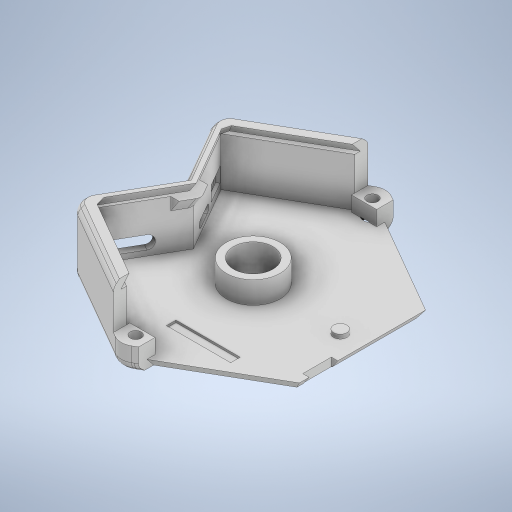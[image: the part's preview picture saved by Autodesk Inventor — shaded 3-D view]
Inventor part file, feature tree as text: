
AUTODESK INVENTOR PART (.ipt)
format: ipt  version: 2024 (Build 280153000, 153)  size: 1,012,224 bytes
history: native  units: in
note: dims shown in document units (in); Inventor stores cm internally (conversion verified against a paired STEP export)
features: extrude x30, move_body x17, direct_edit x9, draft x6, sketch x4, fillet x3, chamfer x2, plane x1
ambient origin geometry x8: Origin, YZ Plane, XZ Plane, XY Plane, X Axis, Y Axis, Z Axis, Center Point
bodies: Solid1 (feature_tree)
feature tree (72):
  extrude  "Extrusion1"  Depth=0.374in
  extrude  "Extrusion2"  Depth=0.0787in TaperAngle=0.0deg
  extrude  "Extrusion3"  Depth=0.6181in TaperAngle=0.0deg
  extrude  "Extrusion6"  Depth=0.0197in
  extrude  "Extrusion9"  Depth=0.0197in
  extrude  "Extrusion11"  Depth=0.0197in
  extrude  "Extrusion12"  Depth=0.0197in
  extrude  "Extrusion13"  TaperAngle=0.0deg  [1 undecoded]
  extrude  "Extrusion14"  Depth=0.0197in
  extrude  "Extrusion15"  Depth=0.0197in
  extrude  "Extrusion16"  Depth=0.0709in
  direct_edit  "Direct Edit2"
  direct_edit  "Direct Edit3"
  extrude  "Extrusion17"  Depth=0.0709in
  extrude  "Extrusion19"  Depth=0.0197in
  extrude  "Extrusion26"  Depth=0.0197in
  extrude  "Extrusion27"  TaperAngle=0.0deg  [1 undecoded]
  sketch  "Sketch19"  dims[d1=0.5098in d2=0.374in]
  extrude  "Extrusion28"  Depth=0.3937in TaperAngle=0.0deg
  extrude  "Extrusion29"  TaperAngle=0.0deg  [1 undecoded]
  draft  "FaceDraft1"
  draft  "FaceDraft2"
  draft  "FaceDraft4"
  sketch  "Sketch20"  dims[d3=0.4449in d7=0.0787in d8=0.0in]
  extrude  "Extrusion30"  Depth=0.3937in TaperAngle=0.0deg
  extrude  "Extrusion31"  Depth=0.0197in TaperAngle=0.0deg
  extrude  "Extrusion32"  Depth=0.0787in
  direct_edit  "Direct Edit5"
  plane  "Work Plane1"
  extrude  "Extrusion37"  Depth=0.0197in TaperAngle=0.0deg
  extrude  "Extrusion38"  Depth=0.0787in
  extrude  "Extrusion39"  Depth=0.0197in TaperAngle=0.0deg
  extrude  "Extrusion40"  Depth=0.0787in TaperAngle=0.0deg
  extrude  "Extrusion42"  TaperAngle=0.0deg  [1 undecoded]
  draft  "FaceDraft5"
  fillet  "Fillet1"  Radius=0.0787in
  draft  "FaceDraft6"
  chamfer  "Chamfer5"  [1 undecoded]
  fillet  "Fillet5"  Radius=0.2405in
  direct_edit  "Direct Edit8"
  direct_edit  "Direct Edit9"
  direct_edit  "Direct Edit10"
  extrude  "Extrusion43"  Depth=0.0787in
  direct_edit  "Direct Edit13"
  direct_edit  "Direct Edit14"
  direct_edit  "Direct Edit15"
  extrude  "Extrusion44"  TaperAngle=0.0deg  [1 undecoded]
  chamfer  "Chamfer6"  [1 undecoded]
  draft  "FaceDraft7"
  fillet  "Fillet6"  Radius=0.3937in
  extrude  "Extrusion45"  Depth=0.0787in
  sketch  "Sketch27"  dims[d21=0.1642in d22=0.1071in d23=0.1142in d24=0.2276in d25=0.1142in d26=0.0in d27=0.0in d38=0.1929in d40=0.1732in d42=0.0709in d43=0.0709in d44=0.6871in d45=0.6871in d46=0.0in d47=0.0in d51=0.3937in d52=0.0in d56=0.0in d57=0.0in d58=0.3937in d59=0.0in d60=0.3976in d61=0.0in d63=0.0787in d64=0.0689in d65=0.0in d66=0.0787in d67=0.0689in d68=0.0in d69=0.0in d70=0.0in d71=0.0787in d72=0.0in d73=0.0in d74=-0.0689in d80=0.0787in d81=0.0in d82=0.0in d85=0.2405in d86=0.0787in d87=0.0in d88=0.0in d118=0.0in d119=0.0in d120=0.3937in d121=0.0in d122=0.0787in d123=30.0deg d124=0.0in d125=0.0in d126=0.3937in d127=0.0in d128=0.2405in d129=-0.2405in d134=0.2405in d135=0.1693in d137=0.0827in d138=0.0in d139=0.0906in d140=0.0in d141=0.0984in d142=0.0in d144=120.0deg d148=0.1575in d154=90.0deg d160=0.1354in d161=0.1378in d179=0.126in d180=0.8268in d181=0.0394in d182=0.0in d183=0.1299in d184=0.1417in d185=0.3937in d186=0.0in d199=0.0in d200=0.0in d201=0.1417in d202=0.0984in d204=0.0394in d205=0.0in d207=120.0deg d211=0.0in d212=0.0in d213=30.0deg d214=-0.2061in d215=0.0492in d216=0.0787in d217=45.0deg d218=0.0787in d219=0.0157in d220=0.0118in d221=0.0in d222=0.0in d223=-0.0059in d224=0.1043in d226=0.0906in d228=0.0in d229=0.0in d230=0.0197in d231=0.0in d232=0.0in d233=-0.0197in d234=0.1535in d235=0.0079in d236=0.1535in d237=0.0906in d239=0.1043in d240=0.0079in d241=0.0295in d242=0.0433in d243=0.0315in d244=0.0335in d247=0.9695in d248=120.0deg d249=0.0295in d250=0.0433in d251=0.065in d253=60.0deg d254=0.0in d255=0.0in d256=0.0157in d258=0.3779in d260=45.0deg d261=45.0deg d262=0.0in d263=0.0in d264=0.0098in d265=0.0in d266=0.0in d267=0.0098in d268=0.1043in d269=0.3937in d270=0.0in d277=0.2224in d278=0.0in d279=0.0in d280=0.0079in d281=0.0in d282=0.0in d283=0.0079in d284=0.0in d285=0.0in d286=0.0059in d287=0.0in d288=0.0in d289=0.0059in d290=0.0in d291=0.0in d292=-0.0039in d293=0.0in d294=0.0in d295=-0.0039in d296=0.0443in d297=0.0in d298=0.0in d299=-0.0079in d300=0.0in d301=0.0in d302=-0.0079in d303=0.0in d304=0.0in d305=-0.0059in d308=30.0deg d310=0.1181in d311=0.0in d312=0.0984in d313=0.0787in d314=45.0deg d315=0.0787in d316=30.0deg d317=0.0787in d318=0.1378in d319=0.2933in d320=0.0906in d321=0.0728in d322=0.6102in d323=0.0197in d324=0.0in d325=0.3937in d326=0.0in d327=0.3937in d328=0.0in d33=0.0197in d34=0.0344in d35=0.0197in d36=0.0344in d62=0.0197in d112=0.0197in d113=0.0344in d114=0.0197in d115=0.0344in d131=0.0197in d132=0.0344in d133=0.0197in d136=0.0344in d166=0.0197in d167=0.0344in d168=0.0197in d169=0.0344in d210=0.0in d225=0.0197in d227=0.0197in d329=0.0197in d330=0.0344in]
  extrude  "Extrusion46"  TaperAngle=30.0deg  [1 undecoded]
  extrude  "Extrusion47"  TaperAngle=0.0deg  [1 undecoded]
  sketch  "Sketch23"  dims[d9=0.2953in d10=0.0in d11=0.6181in d12=0.0in]
  move_body  "Move2"
  move_body  "Move3"
  move_body  "Move15"
  move_body  "Move16"
  move_body  "Move17"
  move_body  "Move18"
  move_body  "Move19"
  move_body  "Move20"
  move_body  "Move23"
  move_body  "Move24"
  move_body  "Move25"
  move_body  "Move26"
  move_body  "Move27"
  move_body  "Move28"
  move_body  "Move29"
  move_body  "Move30"
  move_body  "Move31"
note: 9 required parameter values undecoded (feature->parameter linkage not recoverable at this tier; creation-order binding heuristic only, values carry confidence <= 0.55)
